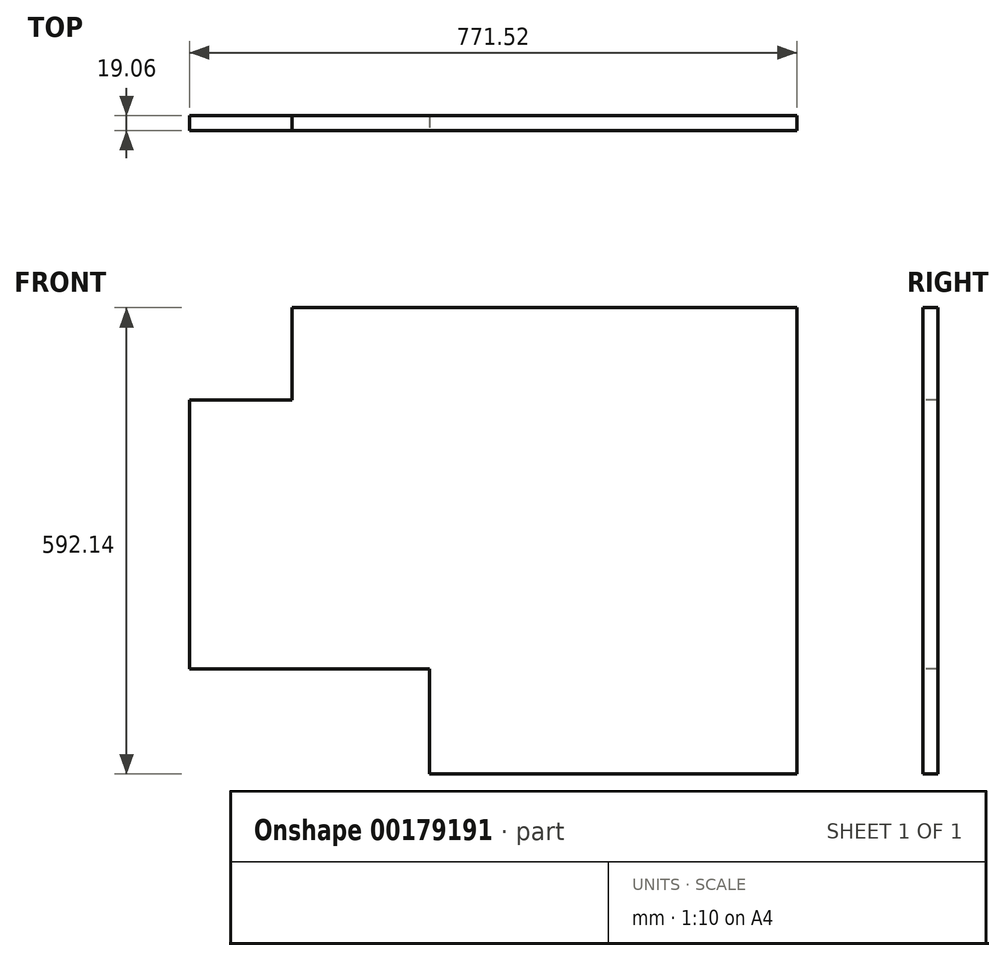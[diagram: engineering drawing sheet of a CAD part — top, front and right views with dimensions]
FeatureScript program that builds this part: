
annotation { "Feature Type Name" : "Feature", "Feature Type Description" : "" }
export const myFeature = defineFeature(function(context is Context, id is Id, definition is map)
    precondition{}
    {
        {
            var Q0;
            Q0=qCreatedBy(makeId("Front.planeOp"),FACE);
            var sketch = newSketch(context, id + "F0", { "sketchPlane" : qUnion([Q0])});
            skLineSegment(sketch, "E0.bottom", {"start": v(-247.9, 296.07) * mm, "end": v(523.62, 296.07) * mm});
            skLineSegment(sketch, "E0.top", {"start": v(-247.9, -296.07) * mm, "end": v(523.62, -296.07) * mm});
            skLineSegment(sketch, "E0.left", {"start": v(-247.9, 296.07) * mm, "end": v(-247.9, -296.07) * mm});
            skLineSegment(sketch, "E0.right", {"start": v(523.62, 296.07) * mm, "end": v(523.62, -296.07) * mm});
            skLineSegment(sketch, "E1", {"start": v(-247.9, 0) * mm, "end": v(523.62, 0) * mm});
            skSolve(sketch);
        }
        {
            var Q0;
            {var subQ0=sQuery(id+"F0.wireOp",EDGE,"E0.bottom");Q0=makeQuery(id+"F0.imprint","IMPRINT",FACE,{"disambiguationData":[TD([[makeQuery(id+"F0.imprint","IMPRINT",EDGE,{"derivedFrom":subQ0}),-1.0]])]});}
            var Q1;
            {var subQ0=sQuery(id+"F0.wireOp",EDGE,"E0.top");Q1=makeQuery(id+"F0.imprint","IMPRINT",FACE,{"disambiguationData":[TD([[makeQuery(id+"F0.imprint","IMPRINT",EDGE,{"derivedFrom":subQ0}),1.0]])]});}
            extrude(context, id + "F1", {"entities" : qUnion([Q0, Q1]), "depth" : 19.05 * mm, "symmetric" : true});
        }
        {
            var Q0;
            Q0=makeQuery(id+"F1.opExtrude","CAP_FACE",FACE,{"disambiguationData":[OSD([sQuery(id+"F0.wireOp",EDGE,"E0.bottom"),sQuery(id+"F0.wireOp",EDGE,"E0.top"),sQuery(id+"F0.wireOp",EDGE,"E0.left"),sQuery(id+"F0.wireOp",EDGE,"E0.right")])],"isStart":false});
            var sketch = newSketch(context, id + "F2", { "sketchPlane" : qUnion([Q0])});
            skLineSegment(sketch, "E2.bottom", {"start": v(-247.9, -296.07) * mm, "end": v(56.9, -296.07) * mm});
            skLineSegment(sketch, "E2.top", {"start": v(-247.9, -162.72) * mm, "end": v(56.9, -162.72) * mm});
            skLineSegment(sketch, "E2.left", {"start": v(-247.9, -296.07) * mm, "end": v(-247.9, -162.72) * mm});
            skLineSegment(sketch, "E2.right", {"start": v(56.9, -296.07) * mm, "end": v(56.9, -162.72) * mm});
            skSolve(sketch);
        }
        {
            var Q0;
            Q0=makeQuery(id+"F2.imprint","IMPRINT",FACE,{"disambiguationData":[TD([[makeQuery(id+"F2.imprint","IMPRINT",EDGE,{"derivedFrom":sQuery(id+"F2.wireOp",EDGE,"E2.bottom")}),1.0]])]});
            extrude(context, id + "F3", {"entities" : qUnion([Q0]), "operationType" : NewBodyOperationType.REMOVE, "endBound" : BoundingType.THROUGH_ALL, "oppositeDirection" : true, "depth" : 25.4 * mm});
        }
        {
            var Q0;
            Q0=makeQuery(id+"F1.opExtrude","CAP_FACE",FACE,{"disambiguationData":[OSD([sQuery(id+"F0.wireOp",EDGE,"E0.bottom"),sQuery(id+"F0.wireOp",EDGE,"E0.top"),sQuery(id+"F0.wireOp",EDGE,"E0.left"),sQuery(id+"F0.wireOp",EDGE,"E0.right")])],"isStart":false});
            var sketch = newSketch(context, id + "F4", { "sketchPlane" : qUnion([Q0])});
            skLineSegment(sketch, "E3.bottom", {"start": v(-247.9, 296.07) * mm, "end": v(-117.73, 296.07) * mm});
            skLineSegment(sketch, "E3.top", {"start": v(-247.9, 178.6) * mm, "end": v(-117.73, 178.6) * mm});
            skLineSegment(sketch, "E3.left", {"start": v(-247.9, 296.07) * mm, "end": v(-247.9, 178.6) * mm});
            skLineSegment(sketch, "E3.right", {"start": v(-117.73, 296.07) * mm, "end": v(-117.73, 178.6) * mm});
            skSolve(sketch);
        }
        {
            var Q0;
            Q0=makeQuery(id+"F4.imprint","IMPRINT",FACE,{"disambiguationData":[TD([[makeQuery(id+"F4.imprint","IMPRINT",EDGE,{"derivedFrom":sQuery(id+"F4.wireOp",EDGE,"E3.bottom")}),-1.0]])]});
            extrude(context, id + "F5", {"entities" : qUnion([Q0]), "operationType" : NewBodyOperationType.REMOVE, "endBound" : BoundingType.THROUGH_ALL, "oppositeDirection" : true, "depth" : 25.4 * mm});
        }
    });
